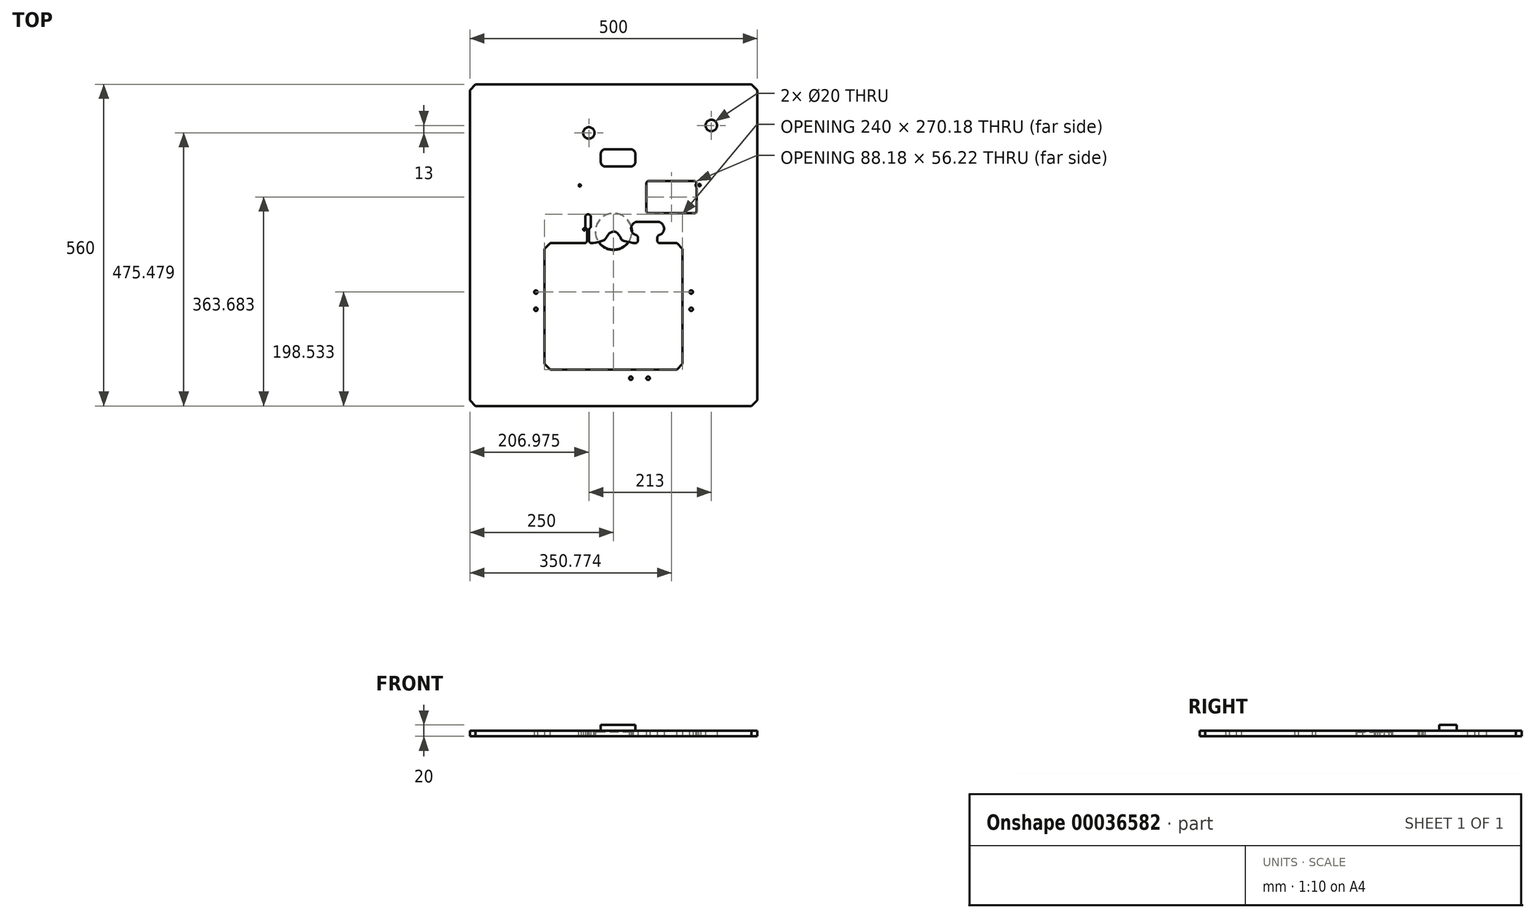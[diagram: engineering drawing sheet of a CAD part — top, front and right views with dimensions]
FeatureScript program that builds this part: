
annotation { "Feature Type Name" : "Feature", "Feature Type Description" : "" }
export const myFeature = defineFeature(function(context is Context, id is Id, definition is map)
    precondition{}
    {
        {
            var Q0;
            Q0=qCreatedBy(makeId("Top.planeOp"),FACE);
            var sketch = newSketch(context, id + "F0", { "sketchPlane" : qUnion([Q0])});
            skFitSpline(sketch, "E0", {"points": [v(-184.92, 256.23) * mm, v(-191.94, 255.14) * mm, v(-205.76, 252.99) * mm, v(-221.68, 237.06) * mm, v(-223.83, 223.24) * mm, v(-224.92, 216.22) * mm]});
            skLineSegment(sketch, "E1", {"start": v(-224.92, 216.22) * mm, "end": v(-224.92, -253.77) * mm});
            skFitSpline(sketch, "E2", {"points": [v(-224.92, -253.77) * mm, v(-223.83, -260.8) * mm, v(-221.68, -274.61) * mm, v(-205.76, -290.54) * mm, v(-191.94, -292.69) * mm, v(-184.92, -293.78) * mm]});
            skLineSegment(sketch, "E3", {"start": v(-184.92, -293.78) * mm, "end": v(185.07, -293.78) * mm});
            skFitSpline(sketch, "E4", {"points": [v(185.07, -293.78) * mm, v(192.1, -292.69) * mm, v(205.91, -290.54) * mm, v(221.84, -274.61) * mm, v(223.99, -260.8) * mm, v(225.08, -253.77) * mm]});
            skLineSegment(sketch, "E5", {"start": v(225.08, -253.77) * mm, "end": v(225.08, 216.22) * mm});
            skFitSpline(sketch, "E6", {"points": [v(225.08, 216.22) * mm, v(223.99, 223.24) * mm, v(221.84, 237.06) * mm, v(205.91, 252.99) * mm, v(192.1, 255.14) * mm, v(185.07, 256.23) * mm]});
            skLineSegment(sketch, "E7", {"start": v(185.07, 256.23) * mm, "end": v(-184.92, 256.23) * mm});
            skFitSpline(sketch, "E8", {"points": [v(165.76, 194.8) * mm, v(165.92, 194.8) * mm, v(166.25, 194.8) * mm, v(166.73, 194.76) * mm, v(167.05, 194.72) * mm, v(167.21, 194.7) * mm]});
            skFitSpline(sketch, "E9", {"points": [v(167.21, 194.7) * mm, v(167.24, 194.72) * mm, v(167.29, 194.75) * mm, v(167.37, 194.8) * mm, v(167.45, 194.8) * mm, v(167.54, 194.8) * mm, v(167.62, 194.75) * mm, v(167.67, 194.72) * mm, v(167.7, 194.7) * mm]});
            skFitSpline(sketch, "E10", {"points": [v(167.7, 194.7) * mm, v(167.85, 194.72) * mm, v(168.17, 194.76) * mm, v(168.66, 194.8) * mm, v(170.81, 194.85) * mm, v(174.65, 193.81) * mm, v(178.65, 189.8) * mm, v(180.14, 184.3) * mm, v(178.65, 178.8) * mm, v(174.65, 174.79) * mm, v(170.81, 173.75) * mm, v(168.66, 173.81) * mm, v(168.17, 173.85) * mm, v(167.85, 173.89) * mm, v(167.7, 173.9) * mm]});
            skFitSpline(sketch, "E11", {"points": [v(167.7, 173.9) * mm, v(167.67, 173.89) * mm, v(167.62, 173.85) * mm, v(167.54, 173.81) * mm, v(167.45, 173.8) * mm, v(167.37, 173.81) * mm, v(167.29, 173.85) * mm, v(167.24, 173.89) * mm, v(167.21, 173.9) * mm]});
            skFitSpline(sketch, "E12", {"points": [v(167.21, 173.9) * mm, v(167.05, 173.89) * mm, v(166.73, 173.85) * mm, v(166.25, 173.81) * mm, v(164.1, 173.75) * mm, v(160.25, 174.8) * mm, v(156.25, 178.8) * mm, v(154.75, 184.3) * mm, v(156.24, 189.76) * mm, v(160.26, 193.94) * mm, v(163.9, 194.51) * mm, v(165.76, 194.8) * mm]});
            skFitSpline(sketch, "E13", {"points": [v(-44.77, 182.08) * mm, v(-44.6, 182.07) * mm, v(-44.28, 182.07) * mm, v(-43.8, 182.03) * mm, v(-43.47, 181.99) * mm, v(-43.31, 181.97) * mm]});
            skFitSpline(sketch, "E14", {"points": [v(-43.31, 181.97) * mm, v(-43.29, 181.99) * mm, v(-43.24, 182.03) * mm, v(-43.16, 182.07) * mm, v(-43.08, 182.08) * mm, v(-43, 182.07) * mm, v(-42.91, 182.03) * mm, v(-42.86, 181.99) * mm, v(-42.84, 181.97) * mm]});
            skFitSpline(sketch, "E15", {"points": [v(-42.84, 181.97) * mm, v(-42.68, 181.99) * mm, v(-42.36, 182.03) * mm, v(-41.87, 182.07) * mm, v(-39.72, 182.12) * mm, v(-35.88, 181.09) * mm, v(-31.88, 177.07) * mm, v(-30.39, 171.57) * mm, v(-31.88, 166.07) * mm, v(-35.88, 162.06) * mm, v(-39.72, 161.03) * mm, v(-41.87, 161.09) * mm, v(-42.36, 161.12) * mm, v(-42.68, 161.16) * mm, v(-42.84, 161.18) * mm]});
            skFitSpline(sketch, "E16", {"points": [v(-42.84, 161.18) * mm, v(-42.86, 161.16) * mm, v(-42.91, 161.12) * mm, v(-43, 161.09) * mm, v(-43.08, 161.07) * mm, v(-43.16, 161.09) * mm, v(-43.24, 161.12) * mm, v(-43.29, 161.16) * mm, v(-43.31, 161.18) * mm]});
            skFitSpline(sketch, "E17", {"points": [v(-43.31, 161.18) * mm, v(-43.47, 161.16) * mm, v(-43.8, 161.12) * mm, v(-44.28, 161.09) * mm, v(-46.43, 161.03) * mm, v(-50.28, 162.06) * mm, v(-54.28, 166.07) * mm, v(-55.78, 171.58) * mm, v(-54.29, 177.04) * mm, v(-50.27, 181.22) * mm, v(-46.62, 181.79) * mm, v(-44.77, 182.08) * mm]});
            skFitSpline(sketch, "E18", {"points": [v(63.06, 87.91) * mm, v(63.2, 87.91) * mm, v(63.49, 87.91) * mm, v(63.93, 87.91) * mm, v(64.23, 87.91) * mm, v(64.39, 87.91) * mm]});
            skFitSpline(sketch, "E19", {"points": [v(137.5, 87.91) * mm, v(138.36, 87.82) * mm, v(140.08, 87.65) * mm, v(142.37, 86.36) * mm, v(143.4, 85.03) * mm, v(143.9, 84.36) * mm]});
            skLineSegment(sketch, "E20", {"start": v(64.39, 87.91) * mm, "end": v(137.5, 87.91) * mm});
            skFitSpline(sketch, "E21", {"points": [v(143.9, 84.36) * mm, v(143.67, 84.02) * mm, v(143.2, 83.34) * mm, v(142.79, 82.12) * mm, v(142.62, 80.66) * mm, v(142.89, 79.02) * mm, v(143.71, 77.39) * mm, v(144.6, 76.61) * mm, v(145.05, 76.22) * mm]});
            skLineSegment(sketch, "E22", {"start": v(145.05, 76.22) * mm, "end": v(145.05, 39.46) * mm});
            skFitSpline(sketch, "E23", {"points": [v(145.05, 39.46) * mm, v(145.32, 37.57) * mm, v(145.73, 34.71) * mm, v(142.23, 31.21) * mm, v(139.37, 31.63) * mm, v(137.5, 31.9) * mm]});
            skLineSegment(sketch, "E24", {"start": v(137.5, 31.9) * mm, "end": v(64.39, 31.9) * mm});
            skFitSpline(sketch, "E25", {"points": [v(64.39, 31.9) * mm, v(62.53, 31.64) * mm, v(59.68, 31.24) * mm, v(56.17, 34.71) * mm, v(56.57, 37.58) * mm, v(56.83, 39.46) * mm]});
            skLineSegment(sketch, "E26", {"start": v(56.83, 39.46) * mm, "end": v(56.83, 80.35) * mm});
            skFitSpline(sketch, "E27", {"points": [v(56.83, 80.35) * mm, v(56.61, 82.1) * mm, v(56.29, 84.75) * mm, v(58.92, 88.39) * mm, v(61.46, 88.1) * mm, v(63.06, 87.91) * mm]});
            skFitSpline(sketch, "E28", {"points": [v(-59.1, 82.42) * mm, v(-59.08, 82.42) * mm, v(-59.03, 82.42) * mm, v(-58.97, 82.41) * mm, v(-58.88, 82.4) * mm, v(-58.77, 82.4) * mm, v(-58.64, 82.36) * mm, v(-58.5, 82.33) * mm, v(-58.39, 82.29) * mm, v(-58.26, 82.24) * mm, v(-58.17, 82.19) * mm, v(-58.1, 82.15) * mm, v(-58.04, 82.11) * mm, v(-57.99, 82.08) * mm, v(-57.94, 82.04) * mm, v(-57.88, 82) * mm, v(-57.83, 81.96) * mm, v(-57.78, 81.92) * mm, v(-57.74, 81.87) * mm, v(-57.66, 81.8) * mm, v(-57.56, 81.69) * mm, v(-57.44, 81.53) * mm, v(-57.35, 81.39) * mm, v(-57.29, 81.25) * mm, v(-57.24, 81.14) * mm, v(-57.2, 81.05) * mm, v(-57.2, 81.01) * mm]});
            skLineSegment(sketch, "E29", {"start": v(-57.2, 81.01) * mm, "end": v(-57.2, 81) * mm});
            skFitSpline(sketch, "E30", {"points": [v(-57.2, 81) * mm, v(-57.18, 80.96) * mm, v(-57.16, 80.88) * mm, v(-57.13, 80.75) * mm, v(-57.12, 80.65) * mm, v(-57.11, 80.56) * mm, v(-57.1, 80.48) * mm, v(-57.1, 80.41) * mm, v(-57.1, 80.35) * mm, v(-57.11, 80.28) * mm, v(-57.12, 80.19) * mm, v(-57.13, 80.08) * mm, v(-57.16, 79.95) * mm, v(-57.2, 79.82) * mm, v(-57.24, 79.7) * mm, v(-57.29, 79.58) * mm, v(-57.35, 79.44) * mm, v(-57.44, 79.3) * mm, v(-57.56, 79.14) * mm, v(-57.67, 79.02) * mm, v(-57.77, 78.92) * mm, v(-57.86, 78.85) * mm, v(-57.93, 78.8) * mm, v(-57.96, 78.78) * mm, v(-57.97, 78.77) * mm, v(-57.98, 78.77) * mm, v(-57.98, 78.76) * mm, v(-57.99, 78.76) * mm, v(-58.04, 78.72) * mm, v(-58.15, 78.66) * mm, v(-58.33, 78.57) * mm, v(-58.49, 78.51) * mm, v(-58.64, 78.47) * mm, v(-58.77, 78.45) * mm, v(-58.88, 78.43) * mm, v(-58.97, 78.42) * mm, v(-59.03, 78.42) * mm, v(-59.1, 78.42) * mm, v(-59.17, 78.42) * mm, v(-59.24, 78.42) * mm, v(-59.28, 78.43) * mm, v(-59.3, 78.43) * mm, v(-59.3, 78.43) * mm, v(-59.36, 78.43) * mm, v(-59.44, 78.45) * mm, v(-59.57, 78.47) * mm, v(-59.65, 78.5) * mm, v(-59.7, 78.5) * mm, v(-59.7, 78.5) * mm, v(-59.72, 78.51) * mm, v(-59.76, 78.53) * mm, v(-59.82, 78.55) * mm, v(-59.86, 78.58) * mm, v(-59.88, 78.58) * mm, v(-59.88, 78.58) * mm, v(-59.9, 78.58) * mm, v(-59.94, 78.6) * mm, v(-60, 78.63) * mm, v(-60.03, 78.66) * mm, v(-60.06, 78.66) * mm, v(-60.06, 78.66) * mm, v(-60.1, 78.66) * mm, v(-60.16, 78.72) * mm, v(-60.26, 78.78) * mm, v(-60.32, 78.83) * mm, v(-60.36, 78.86) * mm, v(-60.37, 78.87) * mm, v(-60.4, 78.89) * mm, v(-60.43, 78.92) * mm, v(-60.47, 78.96) * mm, v(-60.51, 79) * mm, v(-60.56, 79.05) * mm, v(-60.6, 79.1) * mm, v(-60.64, 79.14) * mm, v(-60.68, 79.2) * mm, v(-60.72, 79.24) * mm, v(-60.75, 79.28) * mm, v(-60.76, 79.3) * mm]});
            skLineSegment(sketch, "E31", {"start": v(-60.76, 79.3) * mm, "end": v(-60.76, 79.3) * mm});
            skFitSpline(sketch, "E32", {"points": [v(-60.76, 79.3) * mm, v(-60.8, 79.36) * mm, v(-60.86, 79.46) * mm, v(-60.95, 79.64) * mm, v(-61.01, 79.8) * mm, v(-61.05, 79.95) * mm, v(-61.08, 80.08) * mm, v(-61.1, 80.19) * mm, v(-61.1, 80.28) * mm, v(-61.1, 80.35) * mm, v(-61.1, 80.42) * mm, v(-61.1, 80.49) * mm, v(-61.1, 80.55) * mm, v(-61.1, 80.6) * mm, v(-61.1, 80.62) * mm, v(-61.1, 80.62) * mm, v(-61.1, 80.67) * mm, v(-61.08, 80.75) * mm, v(-61.05, 80.88) * mm, v(-61.03, 80.96) * mm, v(-61.02, 81) * mm]});
            skLineSegment(sketch, "E33", {"start": v(-61.02, 81) * mm, "end": v(-61.02, 81.01) * mm});
            skFitSpline(sketch, "E34", {"points": [v(-61.02, 81.01) * mm, v(-61, 81.03) * mm, v(-61, 81.07) * mm, v(-60.97, 81.13) * mm, v(-60.95, 81.17) * mm, v(-60.94, 81.19) * mm]});
            skLineSegment(sketch, "E35", {"start": v(-60.94, 81.19) * mm, "end": v(-60.94, 81.2) * mm});
            skFitSpline(sketch, "E36", {"points": [v(-60.94, 81.2) * mm, v(-60.94, 81.22) * mm, v(-60.92, 81.26) * mm, v(-60.9, 81.31) * mm, v(-60.87, 81.35) * mm, v(-60.87, 81.37) * mm]});
            skLineSegment(sketch, "E37", {"start": v(-60.87, 81.37) * mm, "end": v(-60.87, 81.37) * mm});
            skFitSpline(sketch, "E38", {"points": [v(-60.87, 81.37) * mm, v(-60.84, 81.41) * mm, v(-60.8, 81.48) * mm, v(-60.72, 81.59) * mm, v(-60.67, 81.65) * mm, v(-60.64, 81.68) * mm]});
            skLineSegment(sketch, "E39", {"start": v(-60.64, 81.68) * mm, "end": v(-60.64, 81.7) * mm});
            skFitSpline(sketch, "E40", {"points": [v(-60.64, 81.7) * mm, v(-60.62, 81.72) * mm, v(-60.56, 81.79) * mm, v(-60.47, 81.87) * mm, v(-60.42, 81.95) * mm, v(-60.38, 81.96) * mm, v(-60.37, 81.96) * mm, v(-60.33, 81.96) * mm, v(-60.28, 82.05) * mm, v(-60.17, 82.11) * mm, v(-60.06, 82.18) * mm, v(-59.94, 82.24) * mm, v(-59.82, 82.29) * mm, v(-59.7, 82.33) * mm, v(-59.57, 82.36) * mm, v(-59.44, 82.4) * mm, v(-59.33, 82.4) * mm, v(-59.24, 82.41) * mm, v(-59.17, 82.42) * mm, v(-59.12, 82.42) * mm, v(-59.1, 82.42) * mm]});
            skLineSegment(sketch, "E41", {"start": v(-44.95, 29.85) * mm, "end": v(-43.75, 29.85) * mm});
            skFitSpline(sketch, "E42", {"points": [v(-43.75, 29.85) * mm, v(-42.97, 29.74) * mm, v(-41.45, 29.52) * mm, v(-39.66, 27.85) * mm, v(-39.42, 26.36) * mm, v(-39.3, 25.62) * mm]});
            skLineSegment(sketch, "E43", {"start": v(-39.3, 25.62) * mm, "end": v(-39.3, 9.4) * mm});
            skFitSpline(sketch, "E44", {"points": [v(-39.3, 9.4) * mm, v(-39.38, 8.75) * mm, v(-39.56, 7.5) * mm, v(-40.86, 5.95) * mm, v(-42.06, 5.5) * mm, v(-42.67, 5.28) * mm]});
            skFitSpline(sketch, "E45", {"points": [v(-33.75, -20.31) * mm, v(-32.18, -19.7) * mm, v(-29.02, -18.49) * mm, v(-24.02, -17.59) * mm, v(-20.76, -16.63) * mm, v(-19.14, -16.15) * mm]});
            skFitSpline(sketch, "E46", {"points": [v(-19.14, -16.15) * mm, v(-18.18, -15.89) * mm, v(-16.28, -15.37) * mm, v(-14, -13.34) * mm, v(-13.12, -11.58) * mm, v(-12.68, -10.7) * mm]});
            skFitSpline(sketch, "E47", {"points": [v(-12.68, -10.7) * mm, v(-11.72, -9.07) * mm, v(-9.82, -5.83) * mm, v(-5.84, -1.54) * mm, v(-2.17, -0.52) * mm, v(-0.34, -0.01) * mm]});
            skFitSpline(sketch, "E48", {"points": [v(-0.34, -0.01) * mm, v(-0.3, 0) * mm, v(-0.2, 0) * mm, v(-0.06, 0) * mm, v(0.03, 0) * mm, v(0.08, 0) * mm]});
            skFitSpline(sketch, "E49", {"points": [v(0.08, 0) * mm, v(1.44, -0.23) * mm, v(4.17, -0.7) * mm, v(7.45, -3.38) * mm, v(9.1, -5.57) * mm, v(9.91, -6.66) * mm]});
            skFitSpline(sketch, "E50", {"points": [v(9.91, -6.66) * mm, v(10.5, -7.53) * mm, v(11.69, -9.28) * mm, v(12.74, -12.28) * mm, v(13.95, -14.02) * mm, v(14.56, -14.88) * mm]});
            skFitSpline(sketch, "E51", {"points": [v(14.56, -14.88) * mm, v(16.48, -15.6) * mm, v(20.32, -17.05) * mm, v(26.4, -18.1) * mm, v(30.4, -19.06) * mm, v(32.38, -19.55) * mm]});
            skLineSegment(sketch, "E52", {"start": v(-42.67, 5.28) * mm, "end": v(-42.67, -20.31) * mm});
            skLineSegment(sketch, "E53", {"start": v(-42.67, -20.31) * mm, "end": v(-33.75, -20.31) * mm});
            skFitSpline(sketch, "E54", {"points": [v(32.38, -19.55) * mm, v(32.61, -19.56) * mm, v(33.06, -19.6) * mm, v(33.66, -19.87) * mm, v(33.96, -20.17) * mm, v(34.11, -20.31) * mm]});
            skFitSpline(sketch, "E55", {"points": [v(42.77, -20.31) * mm, v(42.76, -20.24) * mm, v(42.72, -20.1) * mm, v(42.7, -19.88) * mm, v(42.68, -19.74) * mm, v(42.68, -19.66) * mm]});
            skFitSpline(sketch, "E56", {"points": [v(42.68, -19.66) * mm, v(42.63, -18.24) * mm, v(42.54, -15.4) * mm, v(42.59, -11.12) * mm, v(42.6, -8.27) * mm, v(42.61, -6.85) * mm]});
            skFitSpline(sketch, "E57", {"points": [v(42.61, -6.85) * mm, v(41.02, -6.6) * mm, v(37.83, -6.1) * mm, v(33.75, -3.15) * mm, v(32.35, -0.24) * mm, v(31.65, 1.21) * mm]});
            skFitSpline(sketch, "E58", {"points": [v(31.65, 1.21) * mm, v(31.33, 3.47) * mm, v(30.7, 7.97) * mm, v(34.68, 14.21) * mm, v(39, 15.6) * mm, v(41.16, 16.3) * mm]});
            skFitSpline(sketch, "E59", {"points": [v(41.16, 16.3) * mm, v(44.92, 16.34) * mm, v(52.45, 16.41) * mm, v(63.74, 16.34) * mm, v(71.26, 16.38) * mm, v(75.02, 16.4) * mm]});
            skFitSpline(sketch, "E60", {"points": [v(75.02, 16.4) * mm, v(75.08, 16.4) * mm, v(75.2, 16.41) * mm, v(75.37, 16.42) * mm, v(77.2, 16.44) * mm, v(80.71, 15.48) * mm, v(84.92, 12.1) * mm, v(86.13, 8.8) * mm, v(86.73, 7.16) * mm]});
            skFitSpline(sketch, "E61", {"points": [v(86.73, 7.16) * mm, v(86.8, 4.91) * mm, v(86.93, 0.42) * mm, v(82.4, -5.3) * mm, v(78.04, -6.3) * mm, v(75.85, -6.8) * mm]});
            skFitSpline(sketch, "E62", {"points": [v(75.85, -6.8) * mm, v(75.82, -7.8) * mm, v(75.75, -9.83) * mm, v(75.8, -12.88) * mm, v(75.8, -14.92) * mm, v(75.8, -15.94) * mm]});
            skLineSegment(sketch, "E63", {"start": v(34.11, -20.31) * mm, "end": v(42.77, -20.31) * mm});
            skFitSpline(sketch, "E64", {"points": [v(75.8, -15.94) * mm, v(75.84, -16.41) * mm, v(75.93, -17.39) * mm, v(75.91, -18.87) * mm, v(75.68, -19.83) * mm, v(75.56, -20.31) * mm]});
            skLineSegment(sketch, "E65", {"start": v(75.56, -20.31) * mm, "end": v(100.08, -20.31) * mm});
            skLineSegment(sketch, "E66", {"start": v(100.08, -20.31) * mm, "end": v(100.08, -20.32) * mm});
            skFitSpline(sketch, "E67", {"points": [v(100.08, -20.32) * mm, v(103.59, -20.87) * mm, v(110.49, -21.96) * mm, v(118.44, -29.92) * mm, v(119.52, -36.82) * mm, v(120.07, -40.32) * mm]});
            skLineSegment(sketch, "E68", {"start": v(120.07, -40.32) * mm, "end": v(120.07, -220.32) * mm});
            skLineSegment(sketch, "E69", {"start": v(120.07, -220.32) * mm, "end": v(120.07, -220.32) * mm});
            skFitSpline(sketch, "E70", {"points": [v(120.07, -220.32) * mm, v(119.52, -223.82) * mm, v(118.43, -230.73) * mm, v(110.47, -238.68) * mm, v(103.57, -239.76) * mm, v(100.06, -240.31) * mm]});
            skLineSegment(sketch, "E71", {"start": v(100.06, -240.31) * mm, "end": v(0.08, -240.31) * mm});
            skLineSegment(sketch, "E72", {"start": v(0.08, -240.31) * mm, "end": v(-99.93, -240.31) * mm});
            skLineSegment(sketch, "E73", {"start": v(-99.93, -240.31) * mm, "end": v(-99.93, -240.3) * mm});
            skFitSpline(sketch, "E74", {"points": [v(-99.93, -240.3) * mm, v(-103.43, -239.76) * mm, v(-110.33, -238.67) * mm, v(-118.29, -230.71) * mm, v(-119.37, -223.8) * mm, v(-119.92, -220.3) * mm]});
            skLineSegment(sketch, "E75", {"start": v(-119.92, -220.3) * mm, "end": v(-119.92, -40.3) * mm});
            skLineSegment(sketch, "E76", {"start": v(-119.92, -40.3) * mm, "end": v(-119.91, -40.3) * mm});
            skFitSpline(sketch, "E77", {"points": [v(-119.91, -40.3) * mm, v(-119.36, -36.8) * mm, v(-118.28, -29.9) * mm, v(-110.32, -21.95) * mm, v(-103.41, -20.86) * mm, v(-99.9, -20.31) * mm]});
            skLineSegment(sketch, "E78", {"start": v(-99.9, -20.31) * mm, "end": v(-46.03, -20.31) * mm});
            skLineSegment(sketch, "E79", {"start": v(-46.03, -20.31) * mm, "end": v(-46.03, 5.28) * mm});
            skFitSpline(sketch, "E80", {"points": [v(-46.03, 5.28) * mm, v(-46.64, 5.5) * mm, v(-47.84, 5.95) * mm, v(-49.14, 7.5) * mm, v(-49.32, 8.75) * mm, v(-49.4, 9.4) * mm]});
            skLineSegment(sketch, "E81", {"start": v(-49.4, 9.4) * mm, "end": v(-49.4, 25.62) * mm});
            skFitSpline(sketch, "E82", {"points": [v(-49.4, 25.62) * mm, v(-49.28, 26.36) * mm, v(-49.04, 27.85) * mm, v(-47.25, 29.52) * mm, v(-45.73, 29.74) * mm, v(-44.95, 29.85) * mm]});
            skSolve(sketch);
        }
        {
            var Q0;
            Q0=qCreatedBy(makeId("Top.planeOp"),FACE);
            var sketch = newSketch(context, id + "F1", { "sketchPlane" : qUnion([Q0])});
            skLineSegment(sketch, "E83.bottom", {"start": v(-250, 256.23) * mm, "end": v(250, 256.23) * mm});
            skLineSegment(sketch, "E83.top", {"start": v(-250, -303.77) * mm, "end": v(250, -303.77) * mm});
            skLineSegment(sketch, "E83.left", {"start": v(-250, 256.23) * mm, "end": v(-250, -303.77) * mm});
            skLineSegment(sketch, "E83.right", {"start": v(250, 256.23) * mm, "end": v(250, -303.77) * mm});
            skCircle(sketch, "E84", {"center": v(-58.88, 80.34) * mm, "radius": 2 * mm});
            skCircle(sketch, "E85", {"center": v(-50.88, 3.84) * mm, "radius": 2 * mm});
            skCircle(sketch, "E86", {"center": v(149.52, 80.84) * mm, "radius": 2 * mm});
            skLineSegment(sketch, "E87.bottom", {"start": v(-120, -20.32) * mm, "end": v(-51.03, -20.32) * mm});
            skLineSegment(sketch, "E87.top", {"start": v(-120, -240.32) * mm, "end": v(120, -240.32) * mm});
            skLineSegment(sketch, "E87.left", {"start": v(-120, -20.32) * mm, "end": v(-120, -240.32) * mm});
            skLineSegment(sketch, "E87.right", {"start": v(120, -20.32) * mm, "end": v(120, -240.32) * mm});
            skLineSegment(sketch, "E88.top", {"start": v(42.3, 17) * mm, "end": v(76.05, 17) * mm});
            skLineSegment(sketch, "E88.left", {"start": v(42.3, -15.32) * mm, "end": v(42.3, -10.8) * mm});
            skLineSegment(sketch, "E88.right", {"start": v(76.05, -15.32) * mm, "end": v(76.05, -10.8) * mm});
            skArc(sketch, "E89", {"start": v(42.3, 17) * mm, "mid": v(30.66, 7) * mm, "end": v(38.8, -6.03) * mm});
            skArc(sketch, "E90", {"start": v(76.05, 17) * mm, "mid": v(87.7, 7) * mm, "end": v(79.56, -6.03) * mm});
            skLineSegment(sketch, "E91.trimOffspring", {"start": v(81.05, -20.32) * mm, "end": v(120, -20.32) * mm});
            skPoint(sketch, "E92.visualSharp", {"position": v(-120, -20.32) * mm});
            skPoint(sketch, "E93.visualSharp", {"position": v(120, -20.32) * mm});
            skPoint(sketch, "E94.visualSharp", {"position": v(120, -240.32) * mm});
            skPoint(sketch, "E95.visualSharp", {"position": v(-120, -240.32) * mm});
            skFitSpline(sketch, "E96", {"points": [v(-35.14, -20.32) * mm, v(-31.47, -19.48) * mm, v(-29.72, -18.87) * mm, v(-27.84, -18.4) * mm, v(-26.36, -18.03) * mm, v(-22.65, -17.08) * mm, v(-18.87, -16.07) * mm, v(-16.75, -15.41) * mm, v(-14.94, -14.12) * mm, v(-13.4, -12.07) * mm, v(-12.15, -9.74) * mm, v(-11.54, -8.8) * mm, v(-10.37, -7) * mm, v(-6.66, -2.72) * mm, v(-3.6, -1.02) * mm, v(0, 0) * mm, v(3.8, -0.94) * mm, v(6.22, -2.46) * mm, v(8.21, -4.45) * mm, v(10.25, -7.1) * mm, v(11.25, -8.83) * mm, v(12.29, -10.78) * mm, v(13.28, -12.95) * mm, v(14.62, -14.9) * mm, v(19.73, -16.54) * mm, v(24.33, -17.67) * mm, v(29, -18.62) * mm, v(33.4, -19.8) * mm, v(34.32, -20.32) * mm], "startDerivative": vector(72.5, 26.3) * mm, "endDerivative": vector(29.22, -24.45) * mm});
            skLineSegment(sketch, "E97.trimOffspring", {"start": v(34.32, -20.32) * mm, "end": v(37.3, -20.32) * mm});
            skLineSegment(sketch, "E98", {"start": v(-46.03, -15.32) * mm, "end": v(-46.03, 2.3) * mm});
            skLineSegment(sketch, "E99", {"start": v(-42.67, -15.32) * mm, "end": v(-42.67, 2.3) * mm});
            skLineSegment(sketch, "E100.trimOffspring", {"start": v(-37.67, -20.32) * mm, "end": v(-35.14, -20.32) * mm});
            skArc(sketch, "E101", {"start": v(-49.4, 9.4) * mm, "mid": v(-48.96, 7.6) * mm, "end": v(-47.83, 6.15) * mm});
            skArc(sketch, "E102", {"start": v(-40.88, 6.15) * mm, "mid": v(-39.74, 7.6) * mm, "end": v(-39.3, 9.4) * mm});
            skArc(sketch, "E103", {"start": v(-44.95, 29.85) * mm, "mid": v(-48.07, 28.66) * mm, "end": v(-49.4, 25.62) * mm});
            skArc(sketch, "E104", {"start": v(-39.3, 25.62) * mm, "mid": v(-40.64, 28.68) * mm, "end": v(-43.77, 29.85) * mm});
            skLineSegment(sketch, "E105", {"start": v(-44.95, 29.85) * mm, "end": v(-43.77, 29.85) * mm});
            skLineSegment(sketch, "E106", {"start": v(-39.3, 25.62) * mm, "end": v(-39.3, 9.4) * mm});
            skLineSegment(sketch, "E107", {"start": v(-49.4, 25.62) * mm, "end": v(-49.4, 9.4) * mm});
            skLineSegment(sketch, "E108.bottom", {"start": v(61.68, 88.02) * mm, "end": v(139.87, 88.02) * mm});
            skLineSegment(sketch, "E108.top", {"start": v(61.68, 31.8) * mm, "end": v(139.87, 31.8) * mm});
            skLineSegment(sketch, "E108.left", {"start": v(56.68, 83.02) * mm, "end": v(56.68, 36.8) * mm});
            skLineSegment(sketch, "E108.right", {"start": v(144.87, 76.13) * mm, "end": v(144.87, 36.8) * mm});
            skPoint(sketch, "E109.visualSharp", {"position": v(56.68, 88.02) * mm});
            skArc(sketch, "E109.filletArc", {"start": v(61.68, 88.02) * mm, "mid": v(58.15, 86.56) * mm, "end": v(56.68, 83.02) * mm});
            skPoint(sketch, "E110.visualSharp", {"position": v(144.87, 88.02) * mm});
            skArc(sketch, "E110.filletArc", {"start": v(144.43, 85.07) * mm, "mid": v(142.58, 87.22) * mm, "end": v(139.87, 88.02) * mm});
            skPoint(sketch, "E111.visualSharp", {"position": v(144.87, 31.8) * mm});
            skArc(sketch, "E111.filletArc", {"start": v(139.87, 31.8) * mm, "mid": v(143.4, 33.27) * mm, "end": v(144.87, 36.8) * mm});
            skPoint(sketch, "E112.visualSharp", {"position": v(56.68, 31.8) * mm});
            skArc(sketch, "E112.filletArc", {"start": v(56.68, 36.8) * mm, "mid": v(58.15, 33.27) * mm, "end": v(61.68, 31.8) * mm});
            skArc(sketch, "E113", {"start": v(144.87, 76.13) * mm, "mid": v(142.9, 80.51) * mm, "end": v(144.43, 85.07) * mm});
            skPoint(sketch, "E114.visualSharp", {"position": v(-250, 256.23) * mm});
            skPoint(sketch, "E115.visualSharp", {"position": v(250, 256.23) * mm});
            skPoint(sketch, "E116.visualSharp", {"position": v(250, -303.77) * mm});
            skPoint(sketch, "E117.visualSharp", {"position": v(-250, -303.77) * mm});
            skCircle(sketch, "E118", {"center": v(-43.02, 171.7) * mm, "radius": 10 * mm});
            skCircle(sketch, "E119", {"center": v(169.98, 184.7) * mm, "radius": 10 * mm});
            skPoint(sketch, "E120.visualSharp", {"position": v(-46.03, -20.32) * mm});
            skArc(sketch, "E120.filletArc", {"start": v(-51.03, -20.32) * mm, "mid": v(-47.5, -18.86) * mm, "end": v(-46.03, -15.32) * mm});
            skPoint(sketch, "E121.visualSharp", {"position": v(-42.67, -20.32) * mm});
            skArc(sketch, "E121.filletArc", {"start": v(-42.67, -15.32) * mm, "mid": v(-41.2, -18.86) * mm, "end": v(-37.67, -20.32) * mm});
            skPoint(sketch, "E122.visualSharp", {"position": v(-42.67, 5.24) * mm});
            skArc(sketch, "E122.filletArc", {"start": v(-40.88, 6.15) * mm, "mid": v(-42.2, 4.43) * mm, "end": v(-42.67, 2.3) * mm});
            skPoint(sketch, "E123.visualSharp", {"position": v(-46.03, 5.24) * mm});
            skArc(sketch, "E123.filletArc", {"start": v(-46.03, 2.3) * mm, "mid": v(-46.5, 4.43) * mm, "end": v(-47.83, 6.15) * mm});
            skPoint(sketch, "E124.visualSharp", {"position": v(42.3, -6.56) * mm});
            skArc(sketch, "E124.filletArc", {"start": v(42.3, -10.8) * mm, "mid": v(41.34, -7.84) * mm, "end": v(38.8, -6.03) * mm});
            skPoint(sketch, "E125.visualSharp", {"position": v(42.3, -20.32) * mm});
            skArc(sketch, "E125.filletArc", {"start": v(37.3, -20.32) * mm, "mid": v(40.84, -18.86) * mm, "end": v(42.3, -15.32) * mm});
            skPoint(sketch, "E126.visualSharp", {"position": v(76.05, -20.32) * mm});
            skArc(sketch, "E126.filletArc", {"start": v(76.05, -15.32) * mm, "mid": v(77.51, -18.86) * mm, "end": v(81.05, -20.32) * mm});
            skPoint(sketch, "E127.visualSharp", {"position": v(76.05, -6.56) * mm});
            skArc(sketch, "E127.filletArc", {"start": v(79.56, -6.03) * mm, "mid": v(77.02, -7.84) * mm, "end": v(76.05, -10.8) * mm});
            skCircle(sketch, "E128", {"center": v(-135, -105.32) * mm, "radius": 3 * mm});
            skCircle(sketch, "E129", {"center": v(135, -105.32) * mm, "radius": 3 * mm});
            skCircle(sketch, "E130", {"center": v(30.08, -255.32) * mm, "radius": 3 * mm});
            skCircle(sketch, "E131", {"center": v(-135, -135.32) * mm, "radius": 3 * mm});
            skCircle(sketch, "E132", {"center": v(135, -135.32) * mm, "radius": 3 * mm});
            skCircle(sketch, "E133", {"center": v(60.08, -255.32) * mm, "radius": 3 * mm});
            skLineSegment(sketch, "E134", {"start": v(60, -39.2) * mm, "end": v(60, -327.07) * mm, "construction": true});
            skLineSegment(sketch, "E135.bottom", {"start": v(38.77, -121.5) * mm, "end": v(-38.77, -121.5) * mm, "construction": true});
            skLineSegment(sketch, "E135.top", {"start": v(38.77, -49.16) * mm, "end": v(-38.77, -49.16) * mm, "construction": true});
            skLineSegment(sketch, "E135.left", {"start": v(38.77, -121.5) * mm, "end": v(38.77, -49.16) * mm, "construction": true});
            skLineSegment(sketch, "E135.right", {"start": v(-38.77, -121.5) * mm, "end": v(-38.77, -49.16) * mm, "construction": true});
            skPoint(sketch, "E135.middle", {"position": v(0, -85.32) * mm});
            skLineSegment(sketch, "E136.bottom", {"start": v(-38, -364.74) * mm, "end": v(187, -364.74) * mm, "construction": true});
            skLineSegment(sketch, "E136.top", {"start": v(-38, -564.74) * mm, "end": v(187, -564.74) * mm, "construction": true});
            skLineSegment(sketch, "E136.left", {"start": v(-38, -364.74) * mm, "end": v(-38, -564.74) * mm, "construction": true});
            skLineSegment(sketch, "E136.right", {"start": v(187, -364.74) * mm, "end": v(187, -564.74) * mm, "construction": true});
            skLineSegment(sketch, "E137.bottom", {"start": v(203.45, -26.89) * mm, "end": v(-84.4, -26.89) * mm, "construction": true});
            skLineSegment(sketch, "E137.top", {"start": v(203.45, 205.71) * mm, "end": v(-84.4, 205.71) * mm, "construction": true});
            skLineSegment(sketch, "E137.left", {"start": v(203.45, -26.89) * mm, "end": v(203.45, 205.71) * mm, "construction": true});
            skLineSegment(sketch, "E137.right", {"start": v(-84.4, -26.89) * mm, "end": v(-84.4, 205.71) * mm, "construction": true});
            skPoint(sketch, "E137.middle", {"position": v(59.52, 89.41) * mm});
            skLineSegment(sketch, "E138.bottom", {"start": v(250, -330.23) * mm, "end": v(-250, -330.23) * mm});
            skLineSegment(sketch, "E138.top", {"start": v(250, -600.23) * mm, "end": v(-250, -600.23) * mm});
            skLineSegment(sketch, "E138.left", {"start": v(250, -330.23) * mm, "end": v(250, -600.23) * mm});
            skLineSegment(sketch, "E138.right", {"start": v(-250, -330.23) * mm, "end": v(-250, -600.23) * mm});
            skPoint(sketch, "E138.middle", {"position": v(0, -465.23) * mm});
            skPoint(sketch, "E138.middle.positionSnap0", {"position": v(0, -303.77) * mm});
            skPoint(sketch, "E138.centerSnap0", {"position": v(0, -303.77) * mm});
            skSolve(sketch);
        }
        {
            var Q0;
            {var subQ7=sQuery(id+"F1.wireOp",EDGE,"E83.bottom");Q0=makeQuery(id+"F1.imprint","IMPRINT",FACE,{"disambiguationData":[TD([[makeQuery(id+"F1.imprint","IMPRINT",EDGE,{"derivedFrom":subQ7}),-1.0]])]});}
            extrude(context, id + "F2", {"entities" : qUnion([Q0]), "depth" : 10 * mm});
        }
        {
            var Q0;
            Q0=makeQuery(id+"F2.opExtrude","CAP_FACE",FACE,{"disambiguationData":[OSD([sQuery(id+"F1.wireOp",EDGE,"E83.bottom"),sQuery(id+"F1.wireOp",EDGE,"E83.top"),sQuery(id+"F1.wireOp",EDGE,"E83.left"),sQuery(id+"F1.wireOp",EDGE,"E83.right"),sQuery(id+"F1.wireOp",EDGE,"E84"),sQuery(id+"F1.wireOp",EDGE,"E85"),sQuery(id+"F1.wireOp",EDGE,"E86"),sQuery(id+"F1.wireOp",EDGE,"E87.bottom"),sQuery(id+"F1.wireOp",EDGE,"E87.top"),sQuery(id+"F1.wireOp",EDGE,"E87.left"),sQuery(id+"F1.wireOp",EDGE,"E87.right"),sQuery(id+"F1.wireOp",EDGE,"E88.top"),sQuery(id+"F1.wireOp",EDGE,"E88.left"),sQuery(id+"F1.wireOp",EDGE,"E88.right"),sQuery(id+"F1.wireOp",EDGE,"E89"),sQuery(id+"F1.wireOp",EDGE,"E90"),sQuery(id+"F1.wireOp",EDGE,"E91.trimOffspring"),sQuery(id+"F1.wireOp",EDGE,"E92.filletArc"),sQuery(id+"F1.wireOp",EDGE,"E93.filletArc"),sQuery(id+"F1.wireOp",EDGE,"E94.filletArc"),sQuery(id+"F1.wireOp",EDGE,"E95.filletArc"),sQuery(id+"F1.wireOp",EDGE,"E96"),sQuery(id+"F1.wireOp",EDGE,"E97.trimOffspring"),sQuery(id+"F1.wireOp",EDGE,"E98"),sQuery(id+"F1.wireOp",EDGE,"E99"),sQuery(id+"F1.wireOp",EDGE,"E101"),sQuery(id+"F1.wireOp",EDGE,"E102"),sQuery(id+"F1.wireOp",EDGE,"E103"),sQuery(id+"F1.wireOp",EDGE,"E104"),sQuery(id+"F1.wireOp",EDGE,"E105"),sQuery(id+"F1.wireOp",EDGE,"E106"),sQuery(id+"F1.wireOp",EDGE,"E107"),sQuery(id+"F1.wireOp",EDGE,"E108.bottom"),sQuery(id+"F1.wireOp",EDGE,"E108.top"),sQuery(id+"F1.wireOp",EDGE,"E108.left"),sQuery(id+"F1.wireOp",EDGE,"E108.right"),sQuery(id+"F1.wireOp",EDGE,"E109.filletArc"),sQuery(id+"F1.wireOp",EDGE,"E110.filletArc"),sQuery(id+"F1.wireOp",EDGE,"E111.filletArc"),sQuery(id+"F1.wireOp",EDGE,"E112.filletArc"),sQuery(id+"F1.wireOp",EDGE,"E113"),sQuery(id+"F1.wireOp",EDGE,"E114.filletArc"),sQuery(id+"F1.wireOp",EDGE,"E115.filletArc"),sQuery(id+"F1.wireOp",EDGE,"E116.filletArc"),sQuery(id+"F1.wireOp",EDGE,"E117.filletArc"),sQuery(id+"F1.wireOp",EDGE,"E118"),sQuery(id+"F1.wireOp",EDGE,"E119"),sQuery(id+"F1.wireOp",EDGE,"IIKz3GsU-BTcc-UsvJ-vAxn-oFZpyKUhdffq"),sQuery(id+"F1.wireOp",EDGE,"1kRMBljy-nmr2-g0Ct-LIaz-hHPOI9Y7jgt5"),sQuery(id+"F1.wireOp",EDGE,"oAg7hbSx-cBK2-8GLX-rK9Q-NQo0sEm5mSu5"),sQuery(id+"F1.wireOp",EDGE,"S4aPAin0-RSl6-J928-0MRE-gmd8aCfvXIZ3"),sQuery(id+"F1.wireOp",EDGE,"E120.filletArc"),sQuery(id+"F1.wireOp",EDGE,"E121.filletArc"),sQuery(id+"F1.wireOp",EDGE,"E122.filletArc"),sQuery(id+"F1.wireOp",EDGE,"E123.filletArc"),sQuery(id+"F1.wireOp",EDGE,"E124.filletArc"),sQuery(id+"F1.wireOp",EDGE,"E125.filletArc"),sQuery(id+"F1.wireOp",EDGE,"E126.filletArc"),sQuery(id+"F1.wireOp",EDGE,"E127.filletArc"),sQuery(id+"F1.wireOp",EDGE,"E128"),sQuery(id+"F1.wireOp",EDGE,"E129"),sQuery(id+"F1.wireOp",EDGE,"E130"),sQuery(id+"F1.wireOp",EDGE,"E131"),sQuery(id+"F1.wireOp",EDGE,"E132"),sQuery(id+"F1.wireOp",EDGE,"E133")])],"isStart":false});
            var sketch = newSketch(context, id + "F3", { "sketchPlane" : qUnion([Q0])});
            skLineSegment(sketch, "E139.bottom", {"start": v(29.74, 143.26) * mm, "end": v(-14.26, 143.26) * mm});
            skLineSegment(sketch, "E139.top", {"start": v(29.74, 113.26) * mm, "end": v(-14.26, 113.26) * mm});
            skLineSegment(sketch, "E139.left", {"start": v(37.74, 135.26) * mm, "end": v(37.74, 121.26) * mm});
            skLineSegment(sketch, "E139.right", {"start": v(-22.26, 135.26) * mm, "end": v(-22.26, 121.26) * mm});
            skPoint(sketch, "E139.middle", {"position": v(7.74, 128.26) * mm});
            skPoint(sketch, "E140.visualSharp", {"position": v(-22.26, 143.26) * mm});
            skArc(sketch, "E140.filletArc", {"start": v(-14.26, 143.26) * mm, "mid": v(-19.92, 140.92) * mm, "end": v(-22.26, 135.26) * mm});
            skPoint(sketch, "E141.visualSharp", {"position": v(37.74, 113.26) * mm});
            skArc(sketch, "E141.filletArc", {"start": v(29.74, 113.26) * mm, "mid": v(35.4, 115.6) * mm, "end": v(37.74, 121.26) * mm});
            skPoint(sketch, "E142.visualSharp", {"position": v(37.74, 143.26) * mm});
            skArc(sketch, "E142.filletArc", {"start": v(37.74, 135.26) * mm, "mid": v(35.4, 140.92) * mm, "end": v(29.74, 143.26) * mm});
            skPoint(sketch, "E143.visualSharp", {"position": v(-22.26, 113.26) * mm});
            skArc(sketch, "E143.filletArc", {"start": v(-22.26, 121.26) * mm, "mid": v(-19.92, 115.6) * mm, "end": v(-14.26, 113.26) * mm});
            skSolve(sketch);
        }
        {
            var Q0;
            Q0 = qSketchRegion(id + "F3", true);
            extrude(context, id + "F4", {"entities" : qUnion([Q0]), "depth" : 10 * mm});
        }
        {
            var Q0;
            Q0=makeQuery(id+"F2.opExtrude","SWEPT_EDGE",EDGE,{"disambiguationData":[OSD([sQuery(id+"F1.wireOp",EDGE,"E87.bottom"),sQuery(id+"F1.wireOp",EDGE,"E87.left")])]});
            var Q1;
            Q1=makeQuery(id+"F2.opExtrude","SWEPT_EDGE",EDGE,{"disambiguationData":[OSD([sQuery(id+"F1.wireOp",EDGE,"E87.right"),sQuery(id+"F1.wireOp",EDGE,"E91.trimOffspring")])]});
            var Q2;
            Q2=makeQuery(id+"F2.opExtrude","SWEPT_EDGE",EDGE,{"disambiguationData":[OSD([sQuery(id+"F1.wireOp",EDGE,"E87.top"),sQuery(id+"F1.wireOp",EDGE,"E87.right")])]});
            var Q3;
            Q3=makeQuery(id+"F2.opExtrude","SWEPT_EDGE",EDGE,{"disambiguationData":[OSD([sQuery(id+"F1.wireOp",EDGE,"E87.top"),sQuery(id+"F1.wireOp",EDGE,"E87.left")])]});
            var Q4;
            Q4=makeQuery(id+"F2.opExtrude","SWEPT_EDGE",EDGE,{"disambiguationData":[OSD([sQuery(id+"F1.wireOp",EDGE,"E83.left"),sQuery(id+"F1.wireOp",EDGE,"g3SpL25Y-xica-iNI3-nMUS-EPaKmJgd56ev.bottom"),sQuery(id+"F1.wireOp",EDGE,"g3SpL25Y-xica-iNI3-nMUS-EPaKmJgd56ev.left")])]});
            var Q5;
            Q5=makeQuery(id+"F2.opExtrude","SWEPT_EDGE",EDGE,{"disambiguationData":[OSD([sQuery(id+"F1.wireOp",EDGE,"E83.left"),sQuery(id+"F1.wireOp",EDGE,"g3SpL25Y-xica-iNI3-nMUS-EPaKmJgd56ev.top"),sQuery(id+"F1.wireOp",EDGE,"g3SpL25Y-xica-iNI3-nMUS-EPaKmJgd56ev.left")])]});
            var Q6;
            Q6=makeQuery(id+"F2.opExtrude","SWEPT_EDGE",EDGE,{"disambiguationData":[OSD([sQuery(id+"F1.wireOp",EDGE,"E83.right"),sQuery(id+"F1.wireOp",EDGE,"EUE5xycL-gcpN-pVhg-6l5N-ySSRRkpqvBHm.bottom"),sQuery(id+"F1.wireOp",EDGE,"EUE5xycL-gcpN-pVhg-6l5N-ySSRRkpqvBHm.left")])]});
            var Q7;
            Q7=makeQuery(id+"F2.opExtrude","SWEPT_EDGE",EDGE,{"disambiguationData":[OSD([sQuery(id+"F1.wireOp",EDGE,"E83.right"),sQuery(id+"F1.wireOp",EDGE,"BAHomVDP-Ras3-ax0Z-elZO-AvndiDLyhn4q.bottom"),sQuery(id+"F1.wireOp",EDGE,"BAHomVDP-Ras3-ax0Z-elZO-AvndiDLyhn4q.left")])]});
            var Q8;
            Q8=makeQuery(id+"F2.opExtrude","SWEPT_EDGE",EDGE,{"disambiguationData":[OSD([sQuery(id+"F1.wireOp",EDGE,"E83.left"),sQuery(id+"F1.wireOp",EDGE,"V1mv2dJQ-oQ6Z-llPZ-QmLM-KX8dSt9u18Eu.bottom"),sQuery(id+"F1.wireOp",EDGE,"V1mv2dJQ-oQ6Z-llPZ-QmLM-KX8dSt9u18Eu.left")])]});
            var Q9;
            Q9=makeQuery(id+"F2.opExtrude","SWEPT_EDGE",EDGE,{"disambiguationData":[OSD([sQuery(id+"F1.wireOp",EDGE,"E83.left"),sQuery(id+"F1.wireOp",EDGE,"V1mv2dJQ-oQ6Z-llPZ-QmLM-KX8dSt9u18Eu.top"),sQuery(id+"F1.wireOp",EDGE,"V1mv2dJQ-oQ6Z-llPZ-QmLM-KX8dSt9u18Eu.left")])]});
            var Q10;
            Q10=makeQuery(id+"F2.opExtrude","SWEPT_EDGE",EDGE,{"disambiguationData":[OSD([sQuery(id+"F1.wireOp",EDGE,"E83.right"),sQuery(id+"F1.wireOp",EDGE,"BAHomVDP-Ras3-ax0Z-elZO-AvndiDLyhn4q.top"),sQuery(id+"F1.wireOp",EDGE,"BAHomVDP-Ras3-ax0Z-elZO-AvndiDLyhn4q.left")])]});
            var Q11;
            Q11=makeQuery(id+"F2.opExtrude","SWEPT_EDGE",EDGE,{"disambiguationData":[OSD([sQuery(id+"F1.wireOp",EDGE,"E83.right"),sQuery(id+"F1.wireOp",EDGE,"EUE5xycL-gcpN-pVhg-6l5N-ySSRRkpqvBHm.top"),sQuery(id+"F1.wireOp",EDGE,"EUE5xycL-gcpN-pVhg-6l5N-ySSRRkpqvBHm.left")])]});
            chamfer(context, id + "F5", {"entities" : qUnion([Q0, Q1, Q2, Q3, Q4, Q5, Q6, Q7, Q8, Q9, Q10, Q11]), "width" : 10 * mm, "tangentPropagation" : true});
        }
        {
            var Q0;
            Q0=qCreatedBy(makeId("Right.planeOp"),FACE);
            var sketch = newSketch(context, id + "F6", { "sketchPlane" : qUnion([Q0])});
            skLineSegment(sketch, "E144", {"start": v(0, 0) * mm, "end": v(32, 0) * mm});
            skLineSegment(sketch, "E145", {"start": v(32, 0) * mm, "end": v(31.5, 7) * mm});
            skLineSegment(sketch, "E146", {"start": v(31.5, 7) * mm, "end": v(0, 7) * mm});
            skLineSegment(sketch, "E147", {"start": v(0, 7) * mm, "end": v(0, 0) * mm});
            skSolve(sketch);
        }
        {
            var Q0;
            Q0=makeQuery(id+"F6.imprint","IMPRINT",FACE,{"disambiguationData":[TD([[makeQuery(id+"F6.imprint","IMPRINT",EDGE,{"derivedFrom":sQuery(id+"F6.wireOp",EDGE,"E144")}),1.0]])]});
            var Q1;
            Q1=sQuery(id+"F6.wireOp",EDGE,"E147");
            revolve(context, id + "F7", {"entities" : qUnion([Q0]), "axis" : qUnion([Q1]), "revolveType" : RevolveType.FULL});
        }
    });
